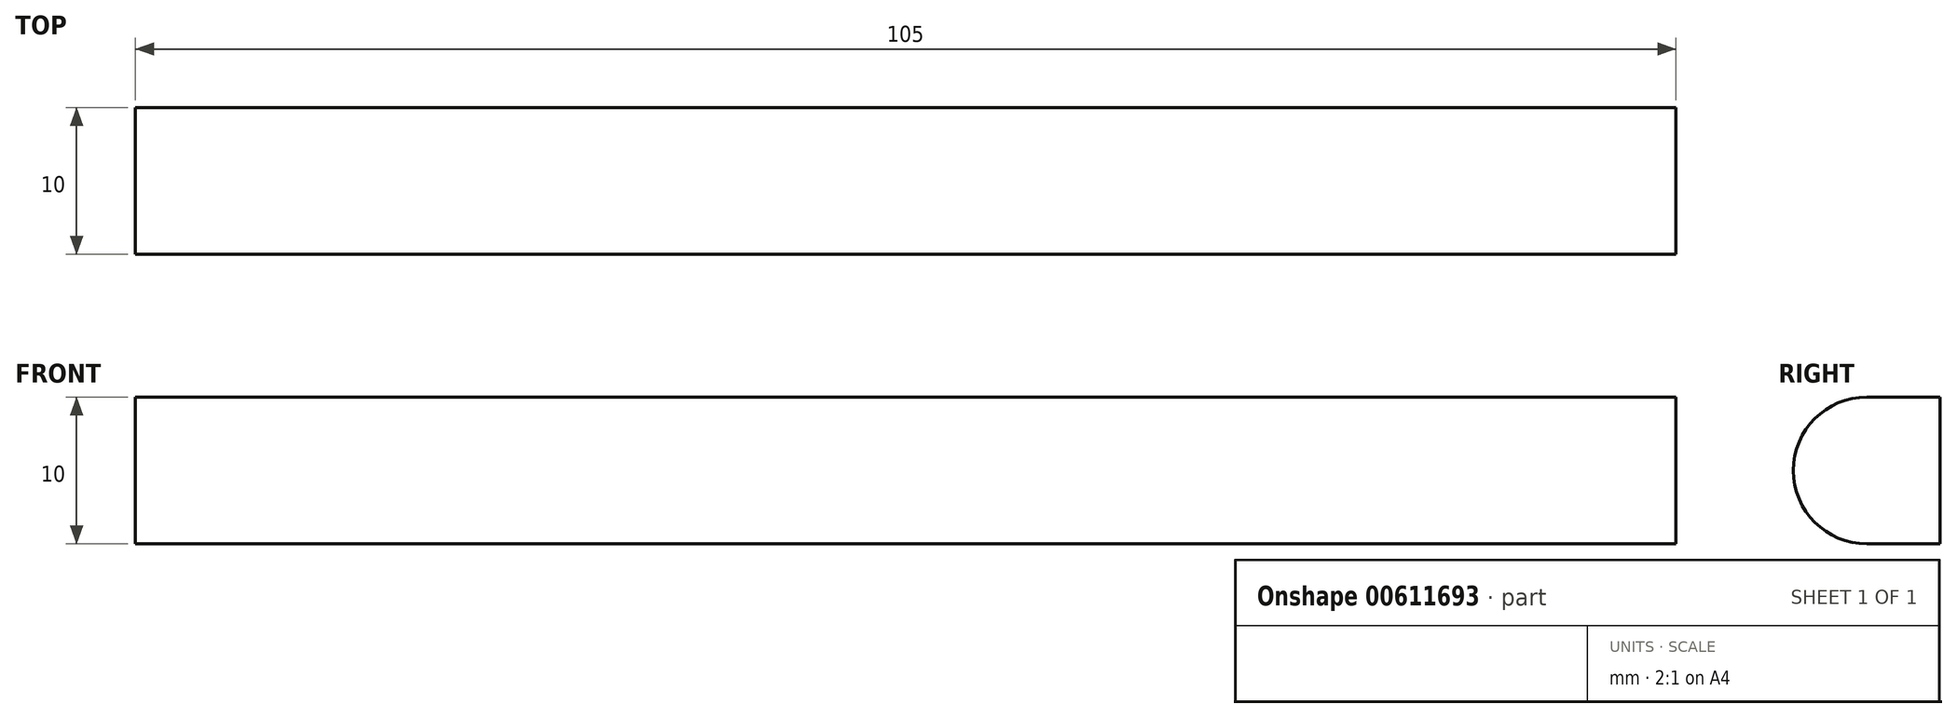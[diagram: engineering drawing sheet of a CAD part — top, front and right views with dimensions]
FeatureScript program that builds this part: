
annotation { "Feature Type Name" : "Feature", "Feature Type Description" : "" }
export const myFeature = defineFeature(function(context is Context, id is Id, definition is map)
    precondition{}
    {
        {
            var Q0;
            Q0=qCreatedBy(makeId("Front.planeOp"),FACE);
            var sketch = newSketch(context, id + "F0", { "sketchPlane" : qUnion([Q0])});
            skLineSegment(sketch, "E0.bottom", {"start": v(52.5, 5) * mm, "end": v(-52.5, 5) * mm});
            skLineSegment(sketch, "E0.top", {"start": v(52.5, -5) * mm, "end": v(-52.5, -5) * mm});
            skLineSegment(sketch, "E0.left", {"start": v(52.5, 5) * mm, "end": v(52.5, -5) * mm});
            skLineSegment(sketch, "E0.right", {"start": v(-52.5, 5) * mm, "end": v(-52.5, -5) * mm});
            skPoint(sketch, "E0.middle", {"position": v(0, 0) * mm});
            skSolve(sketch);
        }
        {
            var Q0;
            Q0=makeQuery(id+"F0.imprint","IMPRINT",FACE,{"disambiguationData":[TD([[makeQuery(id+"F0.imprint","IMPRINT",EDGE,{"derivedFrom":sQuery(id+"F0.wireOp",EDGE,"E0.bottom")}),1.0]])]});
            extrude(context, id + "F1", {"entities" : qUnion([Q0]), "depth" : 10 * mm, "offsetDistance" : 25 * mm});
        }
        {
            var Q0;
            Q0=makeQuery(id+"F1.opExtrude","CAP_EDGE",EDGE,{"disambiguationData":[OSD([sQuery(id+"F0.wireOp",EDGE,"E0.top")])],"isStart":false});
            var Q1;
            Q1=makeQuery(id+"F1.opExtrude","CAP_EDGE",EDGE,{"disambiguationData":[OSD([sQuery(id+"F0.wireOp",EDGE,"E0.bottom")])],"isStart":false});
            fillet(context, id + "F2", {"entities" : qUnion([Q0, Q1]), "radius" : 5 * mm, "tangentPropagation" : true, "allowEdgeOverflow" : false});
        }
    });
